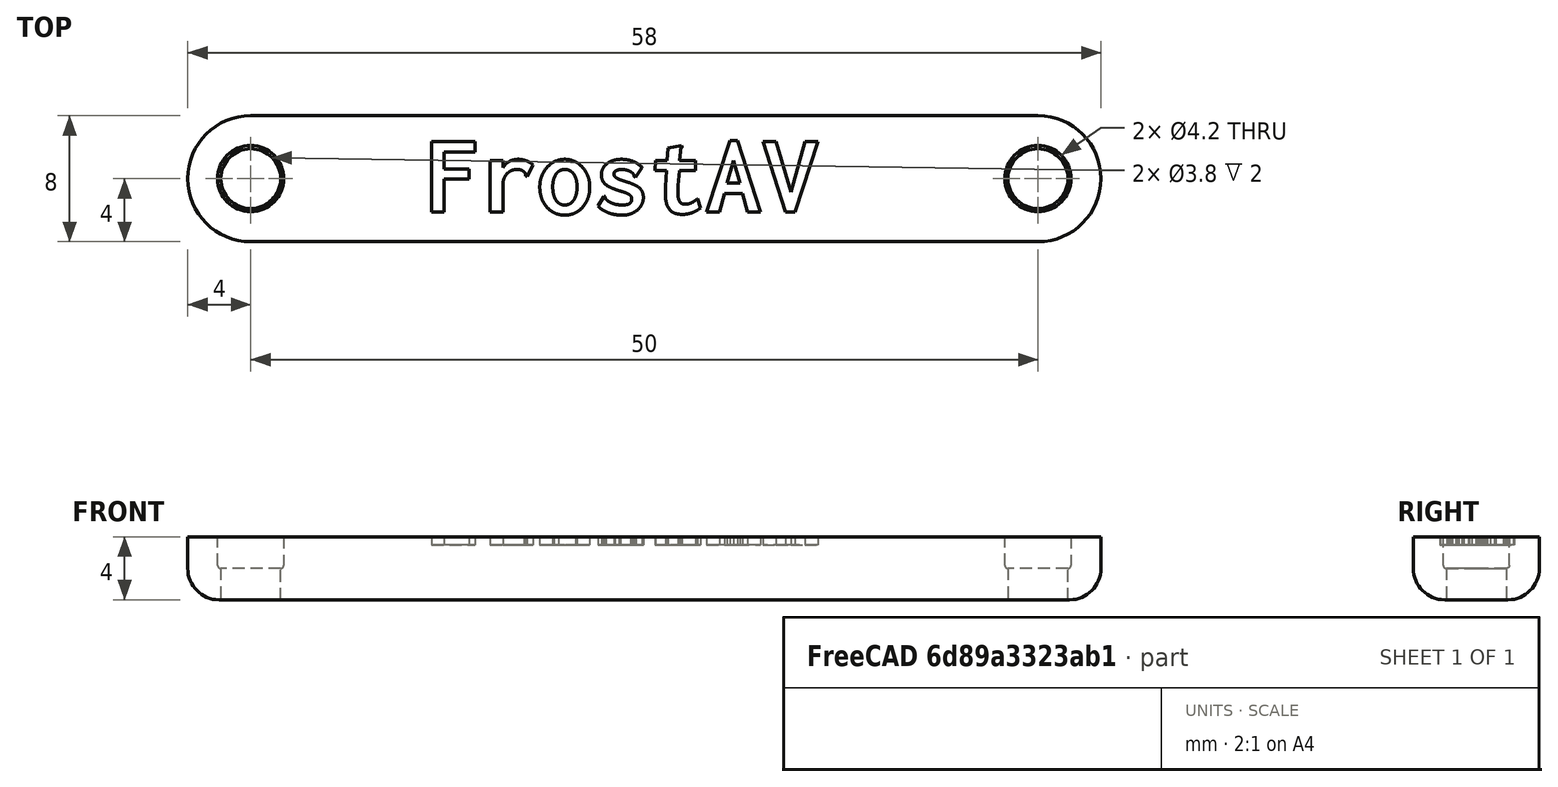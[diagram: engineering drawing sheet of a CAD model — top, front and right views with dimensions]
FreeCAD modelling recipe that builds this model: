
FCSTD DOCUMENT  (FreeCAD 0.18R16146 (Git))
Label: linkage
License: All rights reserved
LicenseURL: http://en.wikipedia.org/wiki/All_rights_reserved
objects: Part::Extrusion×3, Part::Fillet×3, Sketcher::SketchObject×2, Part::Cut×2, Mesh::Feature×1, Part::Part2DObjectPython×1
note: 11 computed .brp shape members not serialized (recipe doc carries the construction recipe); baked Part::Feature solids carry a one-line shape summary decoded from their .brp

FEATURE [Sketcher::SketchObject] Sketch
  sketch-geometry (6):
    g0: LineSegment StartX=0 StartY=0 StartZ=0 EndX=58 EndY=0 EndZ=0
    g1: LineSegment StartX=58 StartY=0 StartZ=0 EndX=58 EndY=8 EndZ=0
    g2: LineSegment StartX=58 StartY=8 StartZ=0 EndX=0 EndY=8 EndZ=0
    g3: LineSegment StartX=0 StartY=8 StartZ=0 EndX=0 EndY=0 EndZ=0
    g4: Circle CenterX=4 CenterY=4 CenterZ=0 NormalX=0 NormalY=0 NormalZ=1 AngleXU=0 Radius=1.9
    g5: Circle CenterX=54 CenterY=4 CenterZ=0 NormalX=0 NormalY=0 NormalZ=1 AngleXU=0 Radius=1.9
  constraints (17):
    c: Coincident(g0,g1)
    c: Coincident(g1,g2)
    c: Coincident(g2,g3)
    c: Coincident(g3,g0)
    c: Horizontal(g0)
    c: Horizontal(g2)
    c: Vertical(g1)
    c: Vertical(g3)
    c: Coincident(g0,g-1)
    c: Distance(g1) = 8
    c: Distance(g4,g2) = 4
    c: Radius(g4) = 1.9
    c: Equal(g4,g5) = 2
    c: Distance(g5,g2) = 4
    c: Distance(g4,g3) = 4
    c: Distance(g5,g1) = 4
    c: Distance(g4,g5) = 50
FEATURE [Part::Extrusion] Extrude
  Base = -> Sketch
  Dir = (0,0,1)
  DirMode = 2
  FaceMakerClass = Part::FaceMakerBullseye
  LengthFwd = 4
  LengthRev = 0
  Solid = true
  Symmetric = false
FEATURE [Part::Fillet] Fillet
  Base = -> Extrude
  Edges = 4 edges r=3.99: [Edge1,Edge2,Edge5,Edge8]
FEATURE [Part::Fillet] Fillet001
  Base = -> Fillet
  Edges = 8 edges r=1.99: [Edge1,Edge5,Edge6,Edge7,Edge8,Edge9,Edge10,Edge11]
FEATURE [Sketcher::SketchObject] Sketch001
  ExternalGeometry = -> [Fillet001]
  MapMode = 5
  Placement = pos=(0,0,4) rot=(0,0,1;0rad)
  Support = -> [Fillet001]
  sketch-geometry (2):
    g0: Circle CenterX=54 CenterY=4 CenterZ=0 NormalX=0 NormalY=0 NormalZ=1 AngleXU=0 Radius=2.1
    g1: Circle CenterX=4 CenterY=4 CenterZ=0 NormalX=0 NormalY=0 NormalZ=1 AngleXU=0 Radius=2.1
  constraints (4):
    c: Coincident(g0,g-3)
    c: Radius(g0) = 2.1
    c: Equal(g0,g1) = 3.25
    c: Coincident(g1,g-4)
FEATURE [Part::Extrusion] Extrude001
  Base = -> Sketch001
  Dir = (0,0,1)
  DirMode = 2
  FaceMakerClass = Part::FaceMakerBullseye
  LengthFwd = -2
  LengthRev = 0
  Solid = true
  Symmetric = false
FEATURE [Part::Cut] Cut
  Base = -> Fillet001
  Tool = -> Extrude001
FEATURE [Mesh::Feature] linkage_new_REV1_3  label="linkage_new_REV1.3"
FEATURE [Part::Fillet] Fillet002
  Base = -> Cut
  Edges = 2 edges r=0.19: [Edge42,Edge44]
FEATURE [Part::Part2DObjectPython] ShapeString  # Draft 2D object (typed FeaturePython)
  FontFile = <path>
  Placement = pos=(15,1.88,4) rot=(0,0,1;0rad)
  Size = 5
  String = FrostAV
  Tracking = 0
FEATURE [Part::Extrusion] Extrude002
  Base = -> ShapeString
  Dir = (0,0,1)
  DirMode = 2
  FaceMakerClass = Part::FaceMakerBullseye
  LengthFwd = -0.5
  LengthRev = 0
  Solid = false
  Symmetric = false
FEATURE [Part::Cut] Cut001
  Base = -> Fillet002
  Tool = -> Extrude002
note: 1 file-system path scrubbed to <path> (originals preserved in the JSON sidecar)
